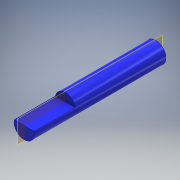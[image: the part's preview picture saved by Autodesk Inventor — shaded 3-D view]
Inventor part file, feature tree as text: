
AUTODESK INVENTOR PART (.ipt)
format: ipt  version: 2017 (Build 210142000, 142)  size: 109,056 bytes
history: native  units: mm
features: extrude x2, sketch x2
ambient origin geometry x8: Origin, YZ Plane, XZ Plane, XY Plane, X Axis, Y Axis, Z Axis, Center Point
bodies: Solid1 (feature_tree)
feature tree (4):
  extrude  "Extrusion1"  Depth=50.8mm TaperAngle=0.0deg
  extrude  "Extrusion2"  Depth=15.875mm
  sketch  "Sketch1"  dims[d0=7.9375mm d1=50.8mm d2=0.0mm]
  sketch  "Sketch2"  dims[d3=15.875mm d4=3.175mm d5=25.4mm d6=0.0mm]
